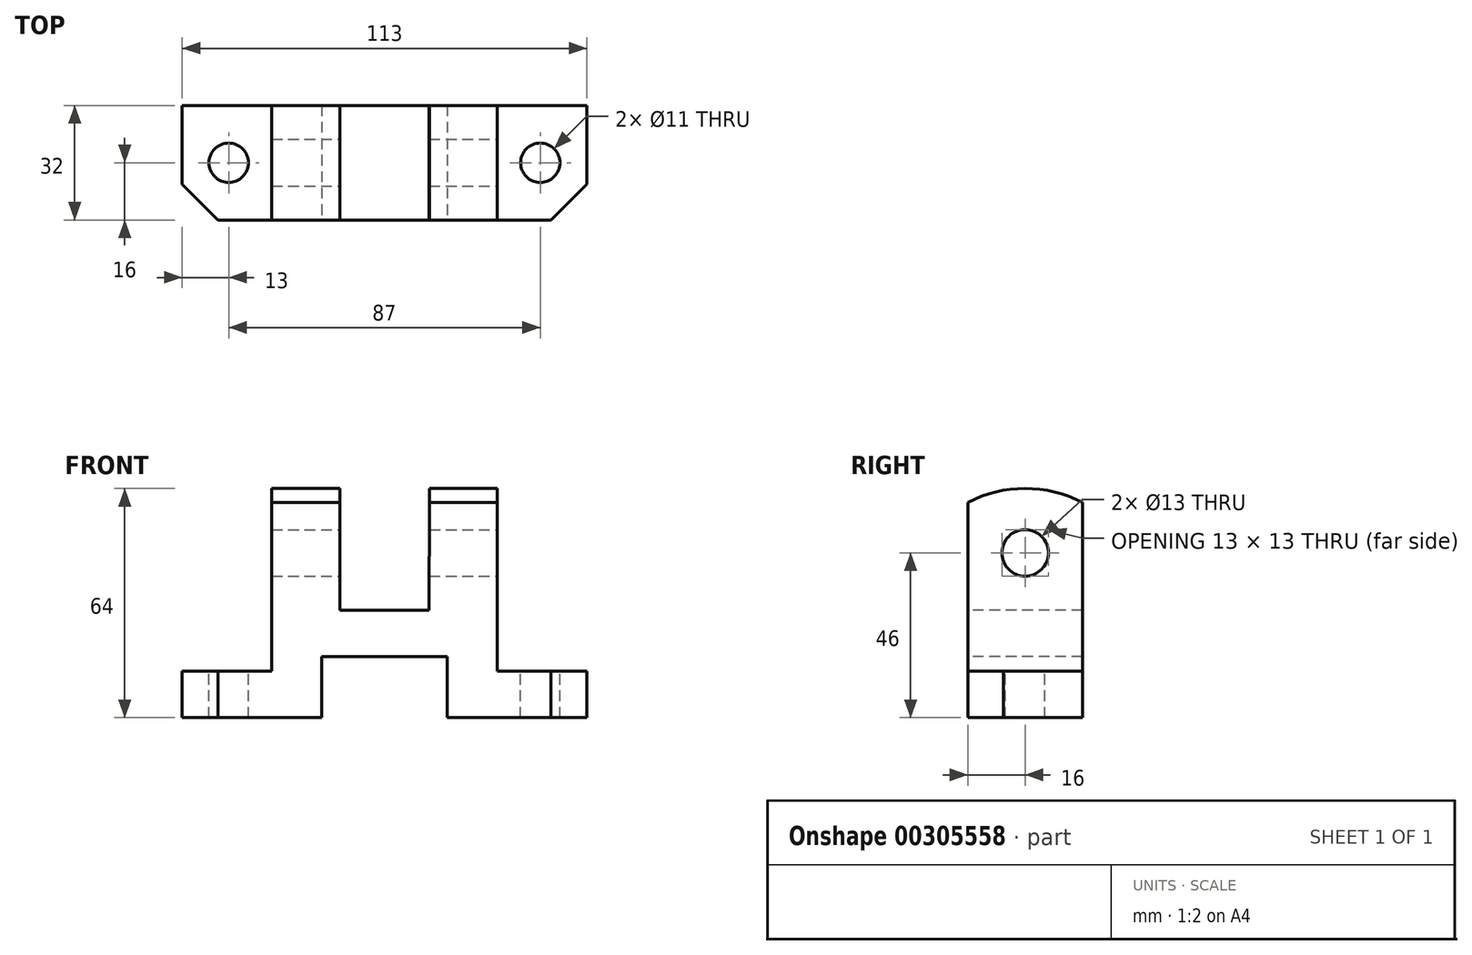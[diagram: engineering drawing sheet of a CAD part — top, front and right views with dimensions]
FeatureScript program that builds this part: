
annotation { "Feature Type Name" : "Feature", "Feature Type Description" : "" }
export const myFeature = defineFeature(function(context is Context, id is Id, definition is map)
    precondition{}
    {
        {
            var Q0;
            Q0=qCreatedBy(makeId("Right.planeOp"),FACE);
            var sketch = newSketch(context, id + "F0", { "sketchPlane" : qUnion([Q0])});
            skLineSegment(sketch, "E0", {"start": v(-16, 31.13) * mm, "end": v(-16, -29) * mm});
            skLineSegment(sketch, "E1", {"start": v(-16, -29) * mm, "end": v(16, -29) * mm});
            skLineSegment(sketch, "E2", {"start": v(16, -29) * mm, "end": v(16, 31.13) * mm});
            skArc(sketch, "E3", {"start": v(16, 31.13) * mm, "mid": v(0, 35) * mm, "end": v(-16, 31.13) * mm});
            skSolve(sketch);
        }
        {
            var Q0;
            Q0 = qSketchRegion(id + "F0", true);
            extrude(context, id + "F1", {"entities" : qUnion([Q0]), "depth" : 113 * mm});
        }
        {
            var Q0;
            Q0=makeQuery(id+"F1.opExtrude","CAP_FACE",FACE,{"disambiguationData":[OSD([sQuery(id+"F0.wireOp",EDGE,"E0"),sQuery(id+"F0.wireOp",EDGE,"E1"),sQuery(id+"F0.wireOp",EDGE,"E2"),sQuery(id+"F0.wireOp",EDGE,"E3")])],"isStart":false});
            var sketch = newSketch(context, id + "F2", { "sketchPlane" : qUnion([Q0])});
            skCircle(sketch, "E4", {"center": v(0, 17) * mm, "radius": 6.5 * mm});
            skSolve(sketch);
        }
        {
            var Q0;
            Q0 = qSketchRegion(id + "F2", true);
            extrude(context, id + "F3", {"entities" : qUnion([Q0]), "operationType" : NewBodyOperationType.REMOVE, "endBound" : BoundingType.THROUGH_ALL, "oppositeDirection" : true, "depth" : 25 * mm});
        }
        {
            var Q0;
            Q0=makeQuery(id+"F1.opExtrude","SWEPT_FACE",FACE,{"disambiguationData":[OSD([sQuery(id+"F0.wireOp",EDGE,"E0")])]});
            var sketch = newSketch(context, id + "F4", { "sketchPlane" : qUnion([Q0])});
            skLineSegment(sketch, "E5", {"start": v(39, -29) * mm, "end": v(74, -29) * mm});
            skLineSegment(sketch, "E6", {"start": v(74, -29) * mm, "end": v(74, -12) * mm});
            skLineSegment(sketch, "E7", {"start": v(74, -12) * mm, "end": v(39, -12) * mm});
            skLineSegment(sketch, "E8", {"start": v(39, -12) * mm, "end": v(39, -29) * mm});
            skLineSegment(sketch, "E9", {"start": v(69, 1) * mm, "end": v(44, 1) * mm});
            skLineSegment(sketch, "E10", {"start": v(44, 1) * mm, "end": v(44, 35.18) * mm});
            skLineSegment(sketch, "E11", {"start": v(44, 35.18) * mm, "end": v(69.1, 35.18) * mm});
            skLineSegment(sketch, "E12", {"start": v(69.1, 35.18) * mm, "end": v(69, 1) * mm});
            skSolve(sketch);
        }
        {
            var Q0;
            Q0 = qSketchRegion(id + "F4", true);
            extrude(context, id + "F5", {"entities" : qUnion([Q0]), "operationType" : NewBodyOperationType.REMOVE, "endBound" : BoundingType.THROUGH_ALL, "oppositeDirection" : true, "depth" : 25 * mm});
        }
        {
            var Q0;
            Q0=qCreatedBy(makeId("Front.planeOp"),FACE);
            var sketch = newSketch(context, id + "F6", { "sketchPlane" : qUnion([Q0])});
            skLineSegment(sketch, "E13", {"start": v(0, -16) * mm, "end": v(25, -16) * mm});
            skLineSegment(sketch, "E14", {"start": v(25, -16) * mm, "end": v(25, 35) * mm});
            skLineSegment(sketch, "E15", {"start": v(25, 35) * mm, "end": v(0, 35) * mm});
            skLineSegment(sketch, "E16", {"start": v(0, 35) * mm, "end": v(0, -16) * mm});
            skLineSegment(sketch, "E17", {"start": v(88.05, 35) * mm, "end": v(113.05, 35) * mm});
            skLineSegment(sketch, "E18", {"start": v(113.05, 35) * mm, "end": v(113.05, -16) * mm});
            skLineSegment(sketch, "E19", {"start": v(113.05, -16) * mm, "end": v(88.05, -16) * mm});
            skLineSegment(sketch, "E20", {"start": v(88.05, -16) * mm, "end": v(88.05, 35) * mm});
            skSolve(sketch);
        }
        {
            var Q0;
            Q0 = qSketchRegion(id + "F6", true);
            extrude(context, id + "F7", {"entities" : qUnion([Q0]), "operationType" : NewBodyOperationType.REMOVE, "endBound" : BoundingType.THROUGH_ALL, "depth" : 25 * mm, "hasSecondDirection" : true, "secondDirectionBound" : SecondDirectionBoundingType.THROUGH_ALL, "secondDirectionOppositeDirection" : true, "secondDirectionDepth" : 25 * mm});
        }
        {
            var Q0;
            Q0=qCreatedBy(makeId("Top.planeOp"),FACE);
            var sketch = newSketch(context, id + "F8", { "sketchPlane" : qUnion([Q0])});
            skLineSegment(sketch, "E21", {"start": v(0, -6) * mm, "end": v(0, -16) * mm});
            skLineSegment(sketch, "E22", {"start": v(0, -16) * mm, "end": v(10, -16) * mm});
            skLineSegment(sketch, "E23", {"start": v(10, -16) * mm, "end": v(0, -6) * mm});
            skCircle(sketch, "E24", {"center": v(13, 0) * mm, "radius": 5.5 * mm});
            skCircle(sketch, "E25", {"center": v(100, 0) * mm, "radius": 5.5 * mm});
            skLineSegment(sketch, "E26", {"start": v(103, -16) * mm, "end": v(113, -16) * mm});
            skLineSegment(sketch, "E27", {"start": v(113, -16) * mm, "end": v(113, -6) * mm});
            skLineSegment(sketch, "E28", {"start": v(113, -6) * mm, "end": v(103, -16) * mm});
            skSolve(sketch);
        }
        {
            var Q0;
            Q0 = qSketchRegion(id + "F8", true);
            extrude(context, id + "F9", {"entities" : qUnion([Q0]), "operationType" : NewBodyOperationType.REMOVE, "endBound" : BoundingType.THROUGH_ALL, "oppositeDirection" : true, "depth" : 25 * mm});
        }
    });
